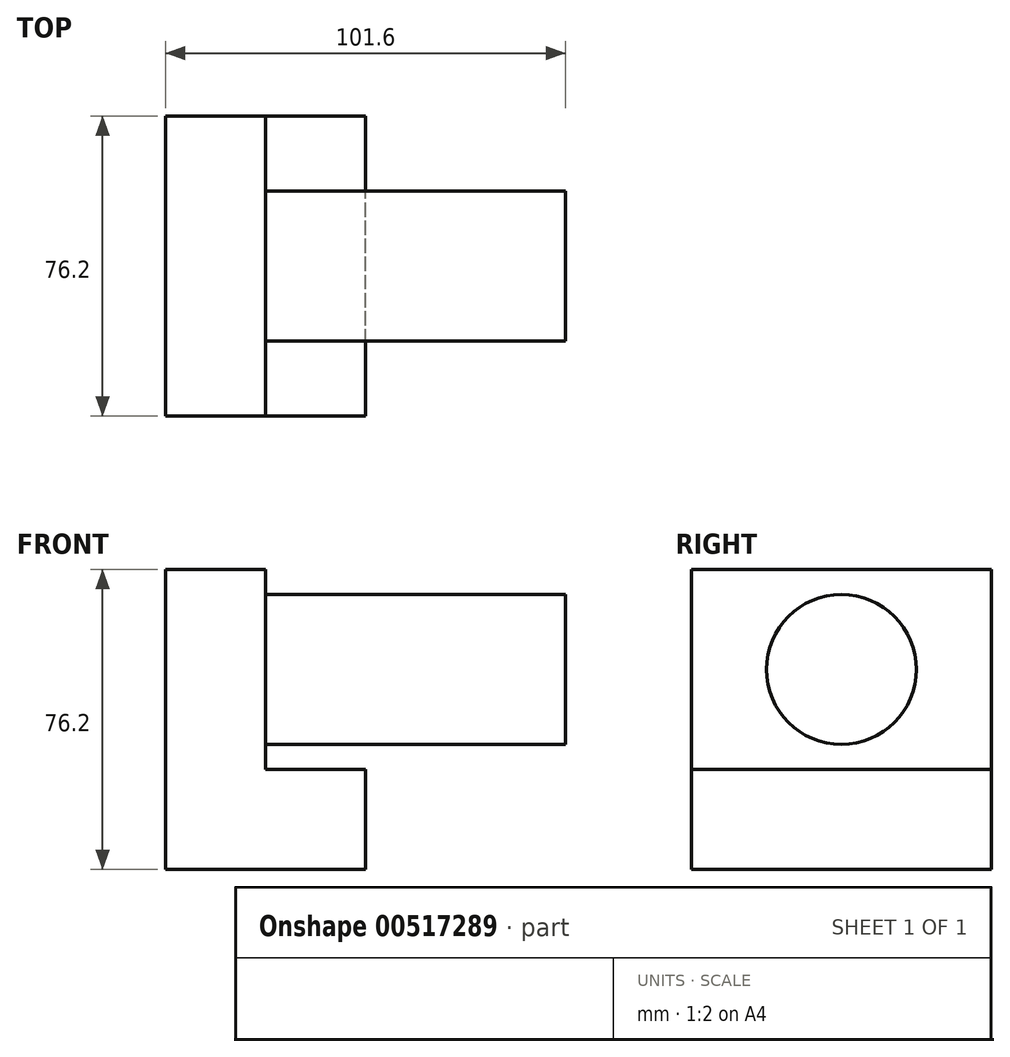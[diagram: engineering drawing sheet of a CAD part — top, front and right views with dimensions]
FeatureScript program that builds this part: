
annotation { "Feature Type Name" : "Feature", "Feature Type Description" : "" }
export const myFeature = defineFeature(function(context is Context, id is Id, definition is map)
    precondition{}
    {
        {
            var Q0;
            Q0=qCreatedBy(makeId("Front.planeOp"),FACE);
            var sketch = newSketch(context, id + "F0", { "sketchPlane" : qUnion([Q0])});
            skLineSegment(sketch, "E0", {"start": v(0, 0) * mm, "end": v(25.4, 0) * mm});
            skLineSegment(sketch, "E1", {"start": v(25.4, 0) * mm, "end": v(25.4, -25.4) * mm});
            skLineSegment(sketch, "E2", {"start": v(25.4, -25.4) * mm, "end": v(-25.4, -25.4) * mm});
            skLineSegment(sketch, "E3", {"start": v(-25.4, -25.4) * mm, "end": v(-25.4, 50.8) * mm});
            skLineSegment(sketch, "E4", {"start": v(-25.4, 50.8) * mm, "end": v(0, 50.8) * mm});
            skLineSegment(sketch, "E5", {"start": v(0, 50.8) * mm, "end": v(0, 0) * mm});
            skSolve(sketch);
        }
        {
            var Q0;
            Q0 = qSketchRegion(id + "F0", true);
            extrude(context, id + "F1", {"entities" : qUnion([Q0]), "depth" : 76.2 * mm, "offsetDistance" : 25.4 * mm});
        }
        {
            var Q0;
            Q0=makeQuery(id+"F1.opExtrude","SWEPT_FACE",FACE,{"disambiguationData":[OSD([sQuery(id+"F0.wireOp",EDGE,"E5")])]});
            var sketch = newSketch(context, id + "F2", { "sketchPlane" : qUnion([Q0])});
            skLineSegment(sketch, "E6", {"start": v(-76.2, 25.4) * mm, "end": v(0, 25.4) * mm, "construction": true});
            skLineSegment(sketch, "E7", {"start": v(-38.1, 25.4) * mm, "end": v(-38.1, 0) * mm});
            skLineSegment(sketch, "E8", {"start": v(-38.1, 0) * mm, "end": v(-38.1, 50.8) * mm, "construction": true});
            skCircle(sketch, "E9", {"center": v(-38.1, 25.4) * mm, "radius": 19.05 * mm});
            skSolve(sketch);
        }
        {
            var Q0;
            Q0 = qSketchRegion(id + "F2", true);
            extrude(context, id + "F3", {"entities" : qUnion([Q0]), "operationType" : NewBodyOperationType.ADD, "depth" : 76.2 * mm, "offsetDistance" : 25.4 * mm});
        }
    });
